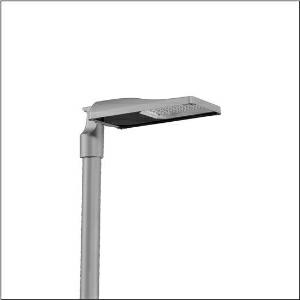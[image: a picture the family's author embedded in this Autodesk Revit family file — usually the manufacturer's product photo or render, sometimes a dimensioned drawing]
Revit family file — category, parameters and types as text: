
# Revit family: streetlight_sl_31_mini___st1_0a_5xh6d3aa08ja_9d22
name_source: partatom
category: Lighting Fixtures
units: mm (PartAtom-declared; Revit-internal decimal feet)

## family parameters
Cut with Voids When Loaded = No
Host = Face
Light Source = No
Part Type = Normal
Room Calculation Point = No
Round Connector Dimension = Use Diameter
Shared = No

## types (1)
- --- (1 x LED, 12140 lm, 81.1 W, 3000K)
    Apparent Load = 81 VA
    CIE Flux Codes = 40 73 97 100 100
    Color Rendering = 70
    Color Temperature = 3000K
    Default Elevation = 1800 mm
    Description = Streetlight SL 31 mini Easy mast luminaire for post-top, side-entry; light control with lens of PMMA; light distribution: ST1.0a, direct asymmetric distribution, for standard-compliant lighting for roads and squares; LED: luminous flux: 12.140lm, light colour: 730, colour temperature: 3000K; luminous efficacy: 149,7lm/W; control: pre-setting: linear dimming characteristic, flexible luminous flux parameterisation, time-dependent luminous flux control, constant luminous flux control, intelligent temperature release in ECG and LED module, overheat protection; luminaire housing, of diecast aluminium, Siteco® metallic grey (DB 702S), corrosivity category C5 high according to DIN EN ISO 12944; cover of toughened safety glass, transparent, opened without tools; mast flange of diecast aluminium, Siteco® metallic grey (DB 702S), spigot size: 76/60mm, mast flange included unmounted; with cable H07RN-F 2x 1.5mm², cable length: 10,5m, connection cable pre-assembled; mains connection: 220..240V, AC, 50/60Hz; power consumption (at start of service life): 81,1W / (at end of service life): 88,3W / (with reduced operation 50%): 36,4W; protection rating (complete): IP66; insulation class (complete): insulation class II (safety insulation); impact resistance: IK10; certification: CE, ENEC, ENEC+, VDE, UKCA; permissible operating ambient temperature for outdoor applications: -40..+50°C; packaging unit: 1 piece

Light Distribution: ST1.0a
    Height = 76 mm
    Lamp = 1 x LED
    Lamp Light Flux = 12140 lm
    Lamp Power = 81.1 W
    Lamp count = 1
    Length = 547 mm
    Luminous efficacy = 150 lm/W
    Manufacturer = Siteco
    ModVariant = No
    Model = 5XH6D3AA08JA
    Number of Poles = 1
    OnlyDefault = Yes
    Power Factor = 1
    Product Name = Streetlight SL 31 mini | ST1.0a
    Product group = mast luminaire | pylon top
    ProductGroupID = 6100
    Protection Class = Protection class II
    Protection Degree = IP 66
    RLX_Detail_Level = 1
    RLX_Emergency_Light_Flux = 0 lm
    RLX_Emergency_Type = 0
    RLX_Emergency_Type_DB = No
    RlxData = <blob elided: 39701 chars, md5=07c7a986>
    Socket = socket
    Standby Power = 0 W
    System Light Flux = 12140 lm
    System Power = 81 W
    Type Comments = factory setting: luminous flux: 100 % | dim-lin: 254 | 860 mA
    Type Image = l_1300326.jpg
    URL = http://relux.com
    VarID = @adj_050486
    Voltage = 0 V
    Weight = 0.00 kg
    Width = 265 mm

## geometry (parser evidence)
native form markers: Blend x4, Sweep x11
no freeform markers — native parametric forms only
